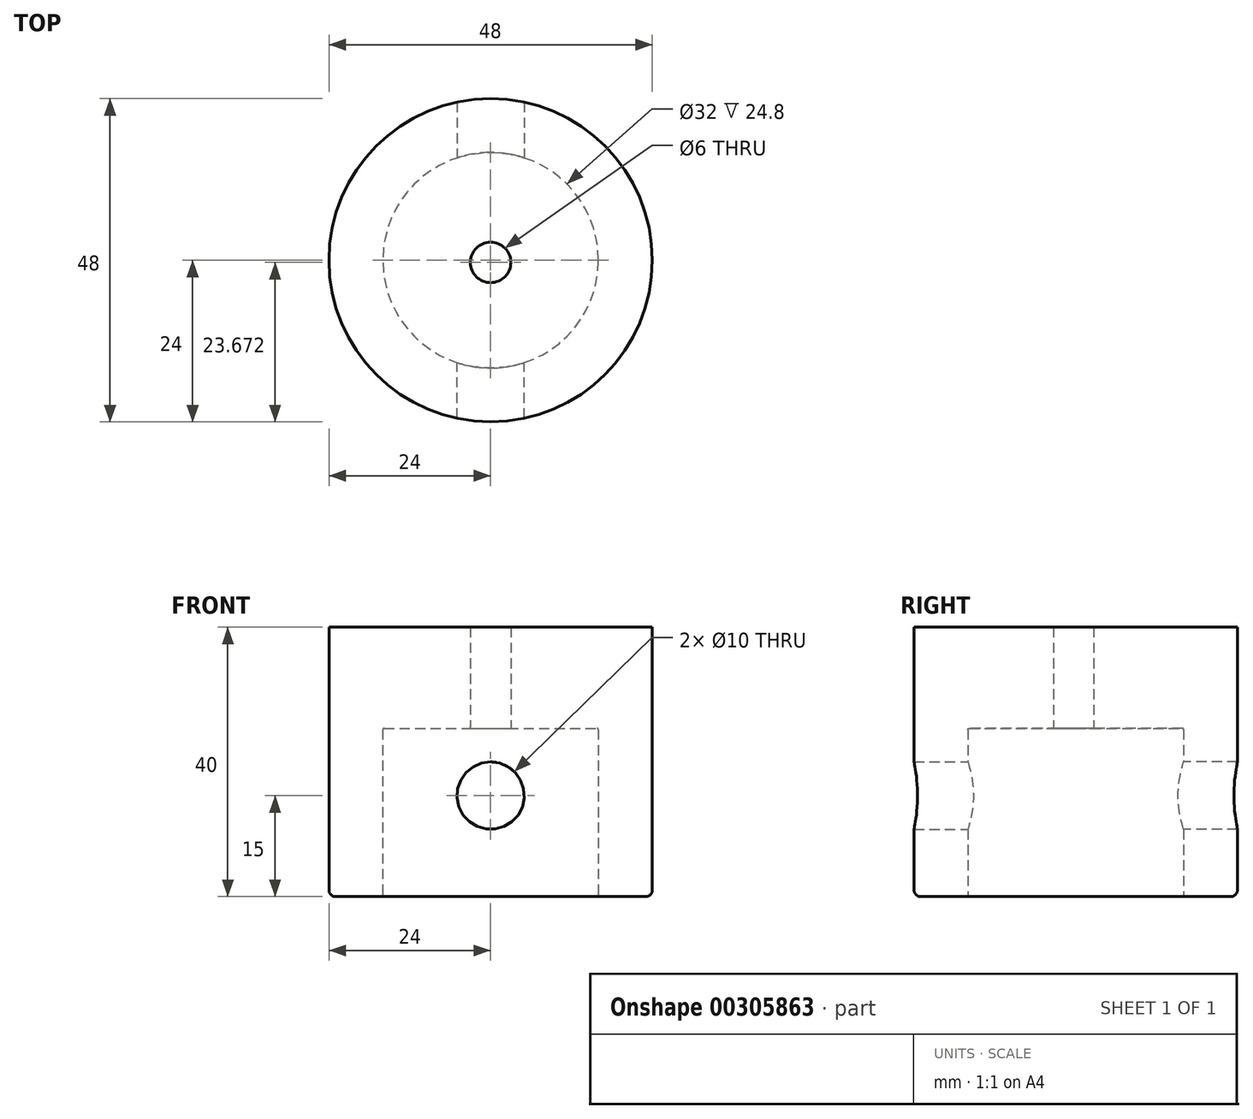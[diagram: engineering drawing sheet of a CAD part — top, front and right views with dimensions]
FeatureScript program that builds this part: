
annotation { "Feature Type Name" : "Feature", "Feature Type Description" : "" }
export const myFeature = defineFeature(function(context is Context, id is Id, definition is map)
    precondition{}
    {
        {
            var Q0;
            Q0=qCreatedBy(makeId("Top.planeOp"),FACE);
            var sketch = newSketch(context, id + "F0", { "sketchPlane" : qUnion([Q0])});
            skCircle(sketch, "E0", {"center": v(0, 0) * mm, "radius": 24 * mm});
            skSolve(sketch);
        }
        {
            var Q0;
            Q0 = qSketchRegion(id + "F0", true);
            extrude(context, id + "F1", {"entities" : qUnion([Q0]), "depth" : 40 * mm});
        }
        {
            var Q0;
            Q0=makeQuery(id+"F1.opExtrude","CAP_FACE",FACE,{"disambiguationData":[OSD([sQuery(id+"F0.wireOp",EDGE,"E0")])],"isStart":true});
            var sketch = newSketch(context, id + "F2", { "sketchPlane" : qUnion([Q0])});
            skCircle(sketch, "E1", {"center": v(0, 0) * mm, "radius": 16 * mm});
            skSolve(sketch);
        }
        {
            var Q0;
            Q0 = qSketchRegion(id + "F2", true);
            extrude(context, id + "F3", {"entities" : qUnion([Q0]), "operationType" : NewBodyOperationType.REMOVE, "oppositeDirection" : true, "depth" : 25 * mm});
        }
        {
            var Q0;
            Q0=makeQuery(id+"F3.boolean.opBoolean","COPY",FACE,{"derivedFrom":makeQuery(id+"F3.opExtrude","CAP_FACE",FACE,{"disambiguationData":[OSD([sQuery(id+"F2.wireOp",EDGE,"E1")])],"isStart":false})});
            var sketch = newSketch(context, id + "F4", { "sketchPlane" : qUnion([Q0])});
            skCircle(sketch, "E2", {"center": v(0, 0.33) * mm, "radius": 3 * mm});
            skSolve(sketch);
        }
        {
            var Q0;
            Q0 = qSketchRegion(id + "F4", true);
            extrude(context, id + "F5", {"entities" : qUnion([Q0]), "operationType" : NewBodyOperationType.REMOVE, "oppositeDirection" : true, "depth" : 25 * mm});
        }
        {
            var Q0;
            Q0=makeQuery(id+"F5.boolean.opBoolean","COPY",EDGE,{"derivedFrom":makeQuery(id+"F5.opExtrude","CAP_EDGE",EDGE,{"disambiguationData":[OSD([sQuery(id+"F4.wireOp",EDGE,"E2")])],"isStart":true})});
            var Q1;
            Q1=makeQuery(id+"F3.boolean.opBoolean","COPY",FACE,{"derivedFrom":makeQuery(id+"F3.opExtrude","CAP_FACE",FACE,{"disambiguationData":[OSD([sQuery(id+"F2.wireOp",EDGE,"E1")])],"isStart":false})});
            fillet(context, id + "F6", {"entities" : qUnion([Q0, Q1]), "radius" : 0.2 * mm, "tangentPropagation" : true, "allowEdgeOverflow" : false});
        }
        {
            var Q0;
            Q0=makeQuery(id+"F3.boolean.opBoolean","COPY",EDGE,{"derivedFrom":makeQuery(id+"F3.opExtrude","CAP_EDGE",EDGE,{"disambiguationData":[OSD([sQuery(id+"F2.wireOp",EDGE,"E1")])],"isStart":true})});
            var Q1;
            Q1=makeQuery(id+"F1.opExtrude","CAP_EDGE",EDGE,{"disambiguationData":[OSD([sQuery(id+"F0.wireOp",EDGE,"E0")])],"isStart":true});
            fillet(context, id + "F7", {"entities" : qUnion([Q0, Q1]), "radius" : 1 * mm, "tangentPropagation" : true, "allowEdgeOverflow" : false});
        }
        {
            var Q0;
            Q0=qCreatedBy(makeId("Front.planeOp"),FACE);
            var sketch = newSketch(context, id + "F8", { "sketchPlane" : qUnion([Q0])});
            skCircle(sketch, "E3", {"center": v(0, 15) * mm, "radius": 5 * mm});
            skSolve(sketch);
        }
        {
            var Q0;
            Q0 = qSketchRegion(id + "F8", true);
            extrude(context, id + "F9", {"entities" : qUnion([Q0]), "operationType" : NewBodyOperationType.REMOVE, "depth" : 50 * mm});
        }
        {
            var Q0;
            Q0=qCreatedBy(makeId("Front.planeOp"),FACE);
            var sketch = newSketch(context, id + "F10", { "sketchPlane" : qUnion([Q0])});
            skCircle(sketch, "E4", {"center": v(0, 15) * mm, "radius": 5 * mm});
            skSolve(sketch);
        }
        {
            var Q0;
            Q0 = qSketchRegion(id + "F10", true);
            extrude(context, id + "F11", {"entities" : qUnion([Q0]), "operationType" : NewBodyOperationType.REMOVE, "oppositeDirection" : true, "depth" : 25 * mm});
        }
    });
